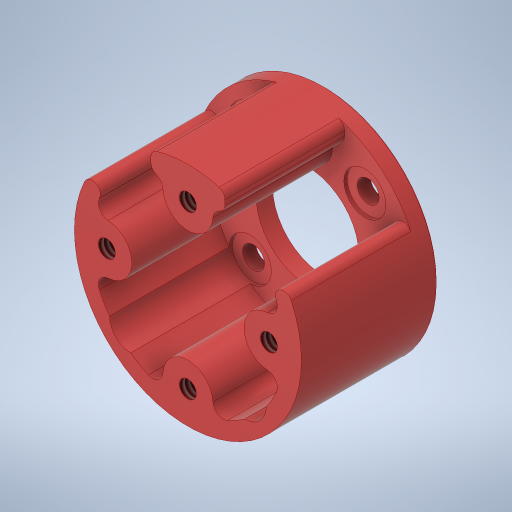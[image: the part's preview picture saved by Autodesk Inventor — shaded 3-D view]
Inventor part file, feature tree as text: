
AUTODESK INVENTOR PART (.ipt)
format: ipt  version: 2023.3 (Build 273359000, 359)  size: 396,288 bytes
history: native  units: in
note: dims shown in document units (in); Inventor stores cm internally (conversion verified against a paired STEP export)
features: sketch x5, extrude x3, hole x2, fillet x2, shell x1, chamfer x1
ambient origin geometry x8: Origin, YZ Plane, XZ Plane, XY Plane, X Axis, Y Axis, Z Axis, Center Point
bodies: Solid1 (feature_tree)
feature tree (14):
  extrude  "Extrusion1"  Depth=0.8268in TaperAngle=0.0deg
  hole  "Hole1"  [1 undecoded]
  shell  "Shell1"  Thickness=0.1in
  fillet  "Fillet1"  Radius=0.0625in
  extrude  "Extrusion2"  Depth=0.05in TaperAngle=0.0deg
  fillet  "Fillet2"  Radius=0.05in
  extrude  "Extrusion3"  TaperAngle=0.0deg  [1 undecoded]
  chamfer  "Chamfer1"  Distance=0.0079in Angle=45.0deg
  hole  "Hole2"  [1 undecoded]
  sketch  "Sketch1"  dims[d0=1.378in d1=0.8268in d2=0.0in]
  sketch  "Sketch2"  dims[d3=0.9843in d4=1.5748in d6=360.0deg]
  sketch  "Sketch3"  dims[d8=0.104in d9=0.276in d10=0.248in d11=0.25in d12=90.0deg d13=1.0in d14=0.8108in d15=0.1in d16=0.0625in]
  sketch  "Sketch4"  dims[d17=0.45in d18=0.7874in d19=0.0in d20=0.05in]
  sketch  "Sketch5"  dims[d21=0.625in d22=0.0in d23=0.0in d24=0.0079in d25=0.125in d26=45.0deg d27=45.0deg d28=1.5748in d30=360.0deg d32=0.134in d33=0.276in d34=0.256in d35=0.0197in d36=90.0deg d37=1.0in d38=0.8108in]
note: 3 required parameter values undecoded (feature->parameter linkage not recoverable at this tier; creation-order binding heuristic only, values carry confidence <= 0.55)
